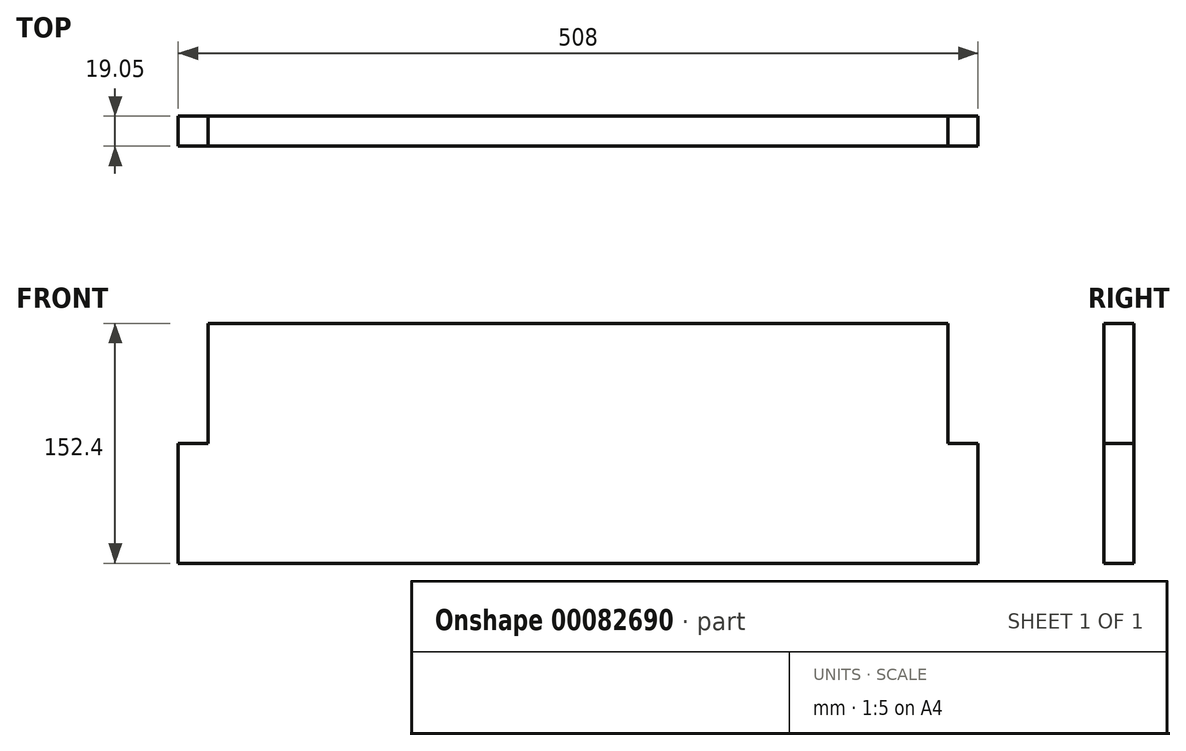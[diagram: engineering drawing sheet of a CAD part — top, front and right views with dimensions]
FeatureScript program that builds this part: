
annotation { "Feature Type Name" : "Feature", "Feature Type Description" : "" }
export const myFeature = defineFeature(function(context is Context, id is Id, definition is map)
    precondition{}
    {
        {
            var Q0;
            Q0=qCreatedBy(makeId("Front.planeOp"),FACE);
            var sketch = newSketch(context, id + "F0", { "sketchPlane" : qUnion([Q0])});
            skLineSegment(sketch, "E0.bottom", {"start": v(-374.45, 6.17) * mm, "end": v(95.45, 6.17) * mm});
            skLineSegment(sketch, "E0.top", {"start": v(-393.5, -146.23) * mm, "end": v(114.5, -146.23) * mm});
            skLineSegment(sketch, "E0.left", {"start": v(-393.5, -70.03) * mm, "end": v(-393.5, -146.23) * mm});
            skLineSegment(sketch, "E0.right", {"start": v(114.5, -70.03) * mm, "end": v(114.5, -146.23) * mm});
            skLineSegment(sketch, "E1.0", {"start": v(-393.5, -70.03) * mm, "end": v(-374.45, -70.03) * mm});
            skLineSegment(sketch, "E2.0", {"start": v(-374.45, 6.17) * mm, "end": v(-374.45, -70.03) * mm});
            skLineSegment(sketch, "E3.0", {"start": v(95.45, 6.17) * mm, "end": v(95.45, -70.03) * mm});
            skLineSegment(sketch, "E4.trimOffspring", {"start": v(95.45, -70.03) * mm, "end": v(114.5, -70.03) * mm});
            skSolve(sketch);
        }
        {
            var Q0;
            Q0=qSketchRegion(id+"F0",true);
            extrude(context, id + "F1", {"entities" : qUnion([Q0]), "depth" : 19.05 * mm});
        }
    });
